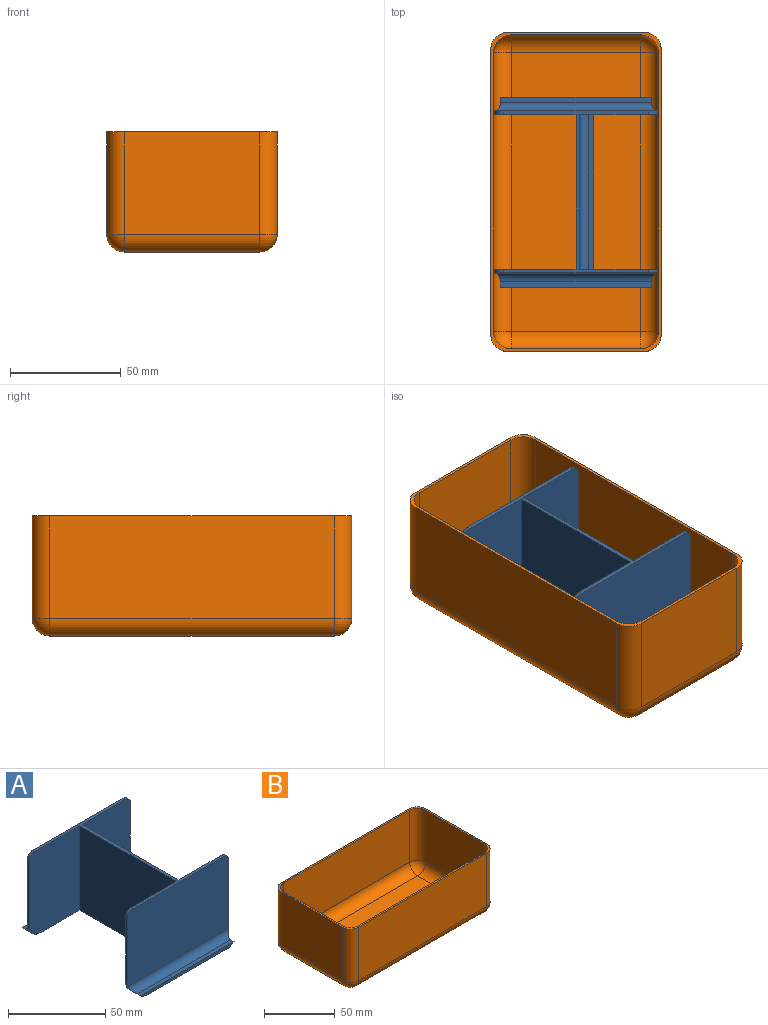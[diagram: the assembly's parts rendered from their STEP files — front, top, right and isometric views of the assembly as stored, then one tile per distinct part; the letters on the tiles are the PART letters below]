
ASSEMBLY  parts=2 mates=1
PART A: 31 faces, bbox 73.5x86x53 mm
  f0: plane 86x57.5mm, normal (0,0,-1), area 1480mm2, adj f1,f5,f6,f7,f10,f13,f14,f17
  f1: plane 70x2mm, normal (1,0,0), area 140mm2, adj f0,f2,f10,f13
  f2: plane 70x2.4mm, normal (0,0,1), area 168mm2, adj f1,f10,f13,f26
  f3: plane 70x47mm, normal (1,0,0), area 3290mm2, adj f4,f10,f13,f26
  f4: plane 73.2x65.5mm, normal (0,0,1), area 321.6mm2, adj f3,f5,f6,f9,f10,f13,f14,f15
  f5: plane 70x53mm, normal (-1,0,0), area 3710mm2, adj f0,f4,f6,f14
  f6: plane 53x36.75mm, normal (0,-1,0), area 1930.6mm2, adj f0,f4,f5,f12,f22,f29
  f7: plane 68.08x2mm, normal (0,1,0), area 129.5mm2, adj f0,f8,f22,f23
  f8: plane 68.08x2.4mm, normal (0,0,1), area 163.4mm2, adj f7,f22,f23,f24
  f9: plane 73.5x47mm, normal (0,1,0), area 3447.3mm2, adj f4,f11,f12,f22,f23,f24,f29,f30
  f10: plane 53x35.15mm, normal (0,-1,0), area 1829.5mm2, adj f0,f1,f2,f3,f4,f11,f23,f26
  f11: plane 41x1.6mm, normal (1,0,0), area 65.6mm2, adj f9,f10,f23,f30
  f12: plane 41x1.6mm, normal (-1,0,0), area 65.6mm2, adj f6,f9,f22,f29
  f13: plane 53x35.15mm, normal (0,1,0), area 1829.5mm2, adj f0,f1,f2,f3,f4,f18,f21,f26
  f14: plane 53x36.75mm, normal (0,1,0), area 1930.6mm2, adj f0,f4,f5,f19,f20,f27
  f15: plane 73.5x47mm, normal (0,-1,0), area 3447.3mm2, adj f4,f18,f19,f20,f21,f25,f27,f28
  f16: plane 68.08x2.4mm, normal (0,0,1), area 163.4mm2, adj f17,f20,f21,f25
  f17: plane 68.08x2mm, normal (0,-1,0), area 129.5mm2, adj f0,f16,f20,f21
  f18: plane 41x1.6mm, normal (1,0,0), area 65.6mm2, adj f13,f15,f21,f28
  f19: plane 41x1.6mm, normal (-1,0,0), area 65.6mm2, adj f14,f15,f20,f27
  f20: cylinder r=8mm len=8mm, axis (0,1,0), area 61.7mm2, adj f0,f14,f15,f16,f17,f19,f25
  f21: cylinder r=8mm len=8mm, axis (0,-1,0), area 61.7mm2, adj f0,f13,f15,f16,f17,f18,f25
  f22: cylinder r=8mm len=8mm, axis (0,1,0), area 61.7mm2, adj f0,f6,f7,f8,f9,f12,f24
  f23: cylinder r=8mm len=8mm, axis (0,-1,0), area 61.7mm2, adj f0,f7,f8,f9,f10,f11,f24
  f24: cylinder r=4mm len=72.99mm, axis (-1,0,0), area 441.9mm2, adj f8,f9,f22,f23
  f25: cylinder r=4mm len=72.99mm, axis (1,0,0), area 441.9mm2, adj f15,f16,f20,f21
  f26: cylinder r=4mm len=70mm, axis (0,1,0), area 439.8mm2, adj f2,f3,f10,f13
  f27: cylinder r=4mm len=4mm, axis (0,-1,0), area 10.1mm2, adj f4,f14,f15,f19
  f28: cylinder r=4mm len=4mm, axis (0,1,0), area 10.1mm2, adj f4,f13,f15,f18
  f29: cylinder r=4mm len=4mm, axis (0,-1,0), area 10.1mm2, adj f4,f6,f9,f12
  f30: cylinder r=4mm len=4mm, axis (0,1,0), area 10.1mm2, adj f4,f9,f10,f11
PART B: 35 faces, bbox 144.6x77.1x54.3 mm
  f0: plane 61.1x46.3mm, normal (1,0,0), area 2828.9mm2, adj f8,f13,f16,f26
  f1: plane 128.6x46.3mm, normal (0,1,0), area 5954.2mm2, adj f8,f13,f14,f22
  f2: plane 61.1x46.3mm, normal (-1,0,0), area 2828.9mm2, adj f8,f14,f15,f19
  f3: plane 58.5x45mm, normal (1,0,0), area 2632.5mm2, adj f8,f9,f12,f32
  f4: plane 126x45mm, normal (0,-1,0), area 5670mm2, adj f8,f9,f10,f28
  f5: plane 58.5x45mm, normal (-1,0,0), area 2632.5mm2, adj f8,f10,f11,f29
  f6: plane 126x45mm, normal (0,1,0), area 5670mm2, adj f8,f11,f12,f33
  f7: plane 128.6x46.3mm, normal (0,-1,0), area 5954.2mm2, adj f8,f15,f16,f23
  f8: plane 144.6x77.1mm, normal (0,0,1), area 569.7mm2, adj f0,f1,f2,f3,f4,f5,f6,f7
  f9: cylinder r=8mm len=45mm, axis (0,0,-1), area 565.5mm2, adj f3,f4,f8,f30
  f10: cylinder r=8mm len=45mm, axis (0,0,1), area 565.5mm2, adj f4,f5,f8,f27
  f11: cylinder r=8mm len=45mm, axis (0,0,-1), area 565.5mm2, adj f5,f6,f8,f31
  f12: cylinder r=8mm len=45mm, axis (0,0,1), area 565.5mm2, adj f3,f6,f8,f34
  f13: cylinder r=8mm len=46.3mm, axis (0,0,-1), area 581.8mm2, adj f0,f1,f8,f24
  f14: cylinder r=8mm len=46.3mm, axis (0,0,1), area 581.8mm2, adj f1,f2,f8,f20
  f15: cylinder r=8mm len=46.3mm, axis (0,0,-1), area 581.8mm2, adj f2,f7,f8,f21
  f16: cylinder r=8mm len=46.3mm, axis (0,0,1), area 581.8mm2, adj f0,f7,f8,f25
  f17: plane 126x58.5mm, normal (0,0,1), area 7371mm2, adj f28,f29,f32,f33
  f18: plane 128.6x61.1mm, normal (0,0,-1), area 7857.5mm2, adj f19,f22,f23,f26
  f19: cylinder r=8mm len=61.1mm, axis (0,-1,0), area 767.8mm2, adj f2,f18,f20,f21
  f20: sphere r=8mm, area 100.5mm2, adj f14,f19,f22
  f21: sphere r=8mm, area 100.5mm2, adj f15,f19,f23
  f22: cylinder r=8mm len=128.6mm, axis (-1,0,0), area 1616mm2, adj f1,f18,f20,f24
  f23: cylinder r=8mm len=128.6mm, axis (1,0,0), area 1616mm2, adj f7,f18,f21,f25
  f24: sphere r=8mm, area 100.5mm2, adj f13,f22,f26
  f25: sphere r=8mm, area 100.5mm2, adj f16,f23,f26
  f26: cylinder r=8mm len=61.1mm, axis (0,1,0), area 767.8mm2, adj f0,f18,f24,f25
  f27: sphere r=8mm, area 100.5mm2, adj f10,f28,f29
  f28: cylinder r=8mm len=126mm, axis (1,0,0), area 1583.4mm2, adj f4,f17,f27,f30
  f29: cylinder r=8mm len=58.5mm, axis (0,-1,0), area 735.1mm2, adj f5,f17,f27,f31
  f30: sphere r=8mm, area 100.5mm2, adj f9,f28,f32
  f31: sphere r=8mm, area 100.5mm2, adj f11,f29,f33
  f32: cylinder r=8mm len=58.5mm, axis (0,1,0), area 735.1mm2, adj f3,f17,f30,f34
  f33: cylinder r=8mm len=126mm, axis (-1,0,0), area 1583.4mm2, adj f6,f17,f31,f34
  f34: sphere r=8mm, area 100.5mm2, adj f12,f32,f33
PLACE A t=(-33.12,-31.53,17.42)mm
PLACE B rot(axis=(0,0,1),90deg) t=(-33.12,-31.53,17.42)mm
MATE revolute A.f0 <-> B.f17  axis (0,0,1) through (-33.12,-31.53,17.42)mm
